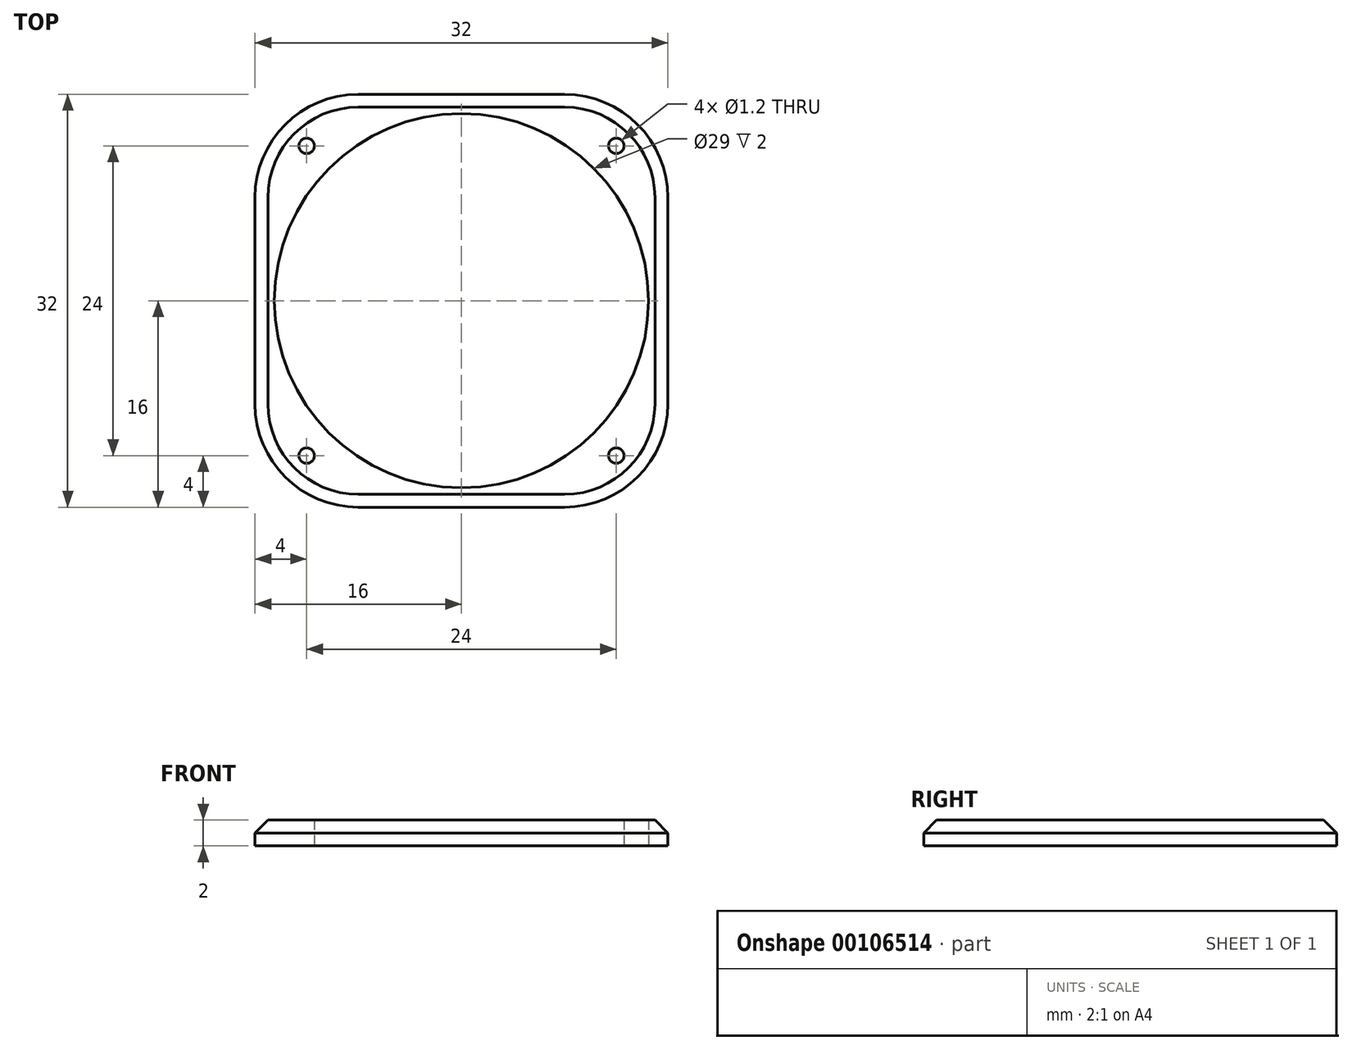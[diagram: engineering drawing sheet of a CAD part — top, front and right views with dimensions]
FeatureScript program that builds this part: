
annotation { "Feature Type Name" : "Feature", "Feature Type Description" : "" }
export const myFeature = defineFeature(function(context is Context, id is Id, definition is map)
    precondition{}
    {
        {
            var Q0;
            Q0=qCreatedBy(makeId("Top.planeOp"),FACE);
            var sketch = newSketch(context, id + "F0", { "sketchPlane" : qUnion([Q0])});
            skLineSegment(sketch, "E0.bottom", {"start": v(0, 0) * mm, "end": v(32, 0) * mm});
            skLineSegment(sketch, "E0.top", {"start": v(0, -32) * mm, "end": v(32, -32) * mm});
            skLineSegment(sketch, "E0.left", {"start": v(0, 0) * mm, "end": v(0, -32) * mm});
            skLineSegment(sketch, "E0.right", {"start": v(32, 0) * mm, "end": v(32, -32) * mm});
            skCircle(sketch, "E1", {"center": v(16, -16) * mm, "radius": 14.5 * mm});
            skLineSegment(sketch, "E2", {"start": v(0, -32) * mm, "end": v(32, 0) * mm, "construction": true});
            skLineSegment(sketch, "E3", {"start": v(28, -4) * mm, "end": v(4, -4) * mm, "construction": true});
            skLineSegment(sketch, "E4", {"start": v(4, -4) * mm, "end": v(4, -28) * mm, "construction": true});
            skLineSegment(sketch, "E5", {"start": v(4, -28) * mm, "end": v(28, -28) * mm, "construction": true});
            skLineSegment(sketch, "E6", {"start": v(28, -28) * mm, "end": v(28, -4) * mm, "construction": true});
            skCircle(sketch, "E7", {"center": v(4, -4) * mm, "radius": 0.6 * mm});
            skCircle(sketch, "E8", {"center": v(28, -4) * mm, "radius": 0.6 * mm});
            skCircle(sketch, "E9", {"center": v(4, -28) * mm, "radius": 0.6 * mm});
            skCircle(sketch, "E10", {"center": v(28, -28) * mm, "radius": 0.6 * mm});
            skLineSegment(sketch, "E11", {"start": v(0, 0) * mm, "end": v(4, -4) * mm});
            skLineSegment(sketch, "E12", {"start": v(28, -28) * mm, "end": v(32, -32) * mm});
            skSolve(sketch);
        }
        {
            var Q0;
            Q0 = qSketchRegion(id + "F0", true);
            extrude(context, id + "F1", {"entities" : qUnion([Q0]), "depth" : 2 * mm});
        }
        {
            var Q0;
            Q0=makeQuery(id+"F1.opExtrude","SWEPT_EDGE",EDGE,{"disambiguationData":[OSD([sQuery(id+"F0.wireOp",EDGE,"E0.bottom"),sQuery(id+"F0.wireOp",EDGE,"E0.right")])]});
            var Q1;
            Q1=makeQuery(id+"F1.opExtrude","SWEPT_EDGE",EDGE,{"disambiguationData":[OSD([sQuery(id+"F0.wireOp",EDGE,"E0.bottom"),sQuery(id+"F0.wireOp",EDGE,"E0.left")])]});
            var Q2;
            Q2=makeQuery(id+"F1.opExtrude","SWEPT_EDGE",EDGE,{"disambiguationData":[OSD([sQuery(id+"F0.wireOp",EDGE,"E0.top"),sQuery(id+"F0.wireOp",EDGE,"E0.left")])]});
            var Q3;
            Q3=makeQuery(id+"F1.opExtrude","SWEPT_EDGE",EDGE,{"disambiguationData":[OSD([sQuery(id+"F0.wireOp",EDGE,"E0.top"),sQuery(id+"F0.wireOp",EDGE,"E0.right")])]});
            fillet(context, id + "F2", {"entities" : qUnion([Q0, Q1, Q2, Q3]), "radius" : 8 * mm, "tangentPropagation" : true, "allowEdgeOverflow" : false});
        }
        {
            var Q0;
            {var subQ0=sQuery(id+"F0.wireOp",EDGE,"E0.left");var subQ1=sQuery(id+"F0.wireOp",EDGE,"E0.bottom");Q0=makeQuery(id+"F2.opFillet","BLEND_EDGE",EDGE,{"blendedFrom":[makeQuery(id+"F1.opExtrude","SWEPT_EDGE",EDGE,{"disambiguationData":[OSD([subQ1,subQ0])]}),makeQuery(id+"F1.opExtrude","CAP_FACE",FACE,{"disambiguationData":[OSD([subQ1,sQuery(id+"F0.wireOp",EDGE,"E0.top"),subQ0,sQuery(id+"F0.wireOp",EDGE,"E0.right"),sQuery(id+"F0.wireOp",EDGE,"E1"),sQuery(id+"F0.wireOp",EDGE,"E7"),sQuery(id+"F0.wireOp",EDGE,"E8"),sQuery(id+"F0.wireOp",EDGE,"E9"),sQuery(id+"F0.wireOp",EDGE,"E10")])],"isStart":false})],"blendedInto":[makeQuery(id+"F1.opExtrude","CAP_FACE",FACE,{"disambiguationData":[OSD([subQ1,sQuery(id+"F0.wireOp",EDGE,"E0.top"),subQ0,sQuery(id+"F0.wireOp",EDGE,"E0.right"),sQuery(id+"F0.wireOp",EDGE,"E1"),sQuery(id+"F0.wireOp",EDGE,"E7"),sQuery(id+"F0.wireOp",EDGE,"E8"),sQuery(id+"F0.wireOp",EDGE,"E9"),sQuery(id+"F0.wireOp",EDGE,"E10")])],"isStart":false})]});}
            chamfer(context, id + "F3", {"entities" : qUnion([Q0]), "width" : 1 * mm, "tangentPropagation" : true});
        }
    });
